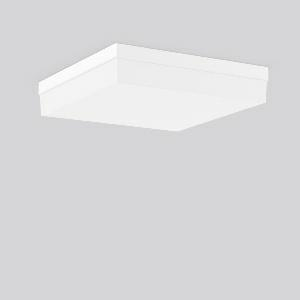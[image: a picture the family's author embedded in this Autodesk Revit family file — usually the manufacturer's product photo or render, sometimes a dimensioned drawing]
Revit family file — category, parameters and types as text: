
# Revit family: flat_quadrat_221162_002_1_f982
name_source: partatom
category: Lighting Fixtures
units: mm (PartAtom-declared; Revit-internal decimal feet)

## family parameters
Cut with Voids When Loaded = No
Host = Face
Light Source = No
Part Type = Normal
Room Calculation Point = No
Round Connector Dimension = Use Diameter
Shared = No

## types (1)
- FLAT QUADRAT (1 x LED Modul 840, 3650 lm, 4000)
    Apparent Load = 54 VA
    CIE Flux Codes = 42 72 91 88 100
    Color Rendering = 80
    Color Temperature = 4000
    Default Elevation = 1800 mm
    Description = Series: FLAT QUADRAT
Flat, square surface-mounted luminaire. Base: plastic. Diffuser: plastic (polypropylene), opal, satin finish. Diffuser fastening: spring system. IP 43 ceiling mounting, IP 44 wall mounting. 
Colour: white
Length: 470 mm
Width: 470 mm
Height: 100 mm
Lamp: LED
Socket: without socket
Colour temperature: 4000K
Colour rendering index (CRI): 83
System power: 54 W
Rated luminous flux: 3650 lm
Luminous efficiency: 68 lm/W
Control gear: Regulated power supply
Protection class: I
Type of protection: IP 43
    Height = 100 mm  [stored 0.328084 ft]
    Lamp = 1 x LED Modul 840
    Lamp Light Flux = 3650 lm
    Lamp count = 1
    Length = 470 mm
    Lifetime = 50000 h
    Luminous efficacy = 68 lm/W
    Manufacturer = RZB
    ModVariant = No
    Model = 221162.002.1
    Mounting Place = Ceiling, Wall
    Mounting Type = Surface mounted
    Number of Poles = 1
    OnlyDefault = Yes
    Power Factor = 1
    Product Name = FLAT QUADRAT
    Product group = Surface mounted ceiling and wall luminaires
    ProductGroupID = 305
    Protection Class = Protection class I
    Protection Degree = IP 43
    RLX_Detail_Level = 1
    RLX_Emergency_Light_Flux = 0 lm
    RLX_Emergency_Type = 0
    RLX_Emergency_Type_DB = No
    RlxData = <blob elided: 13965 chars, md5=58c8b692>
    Socket = socket
    Standby Power = 0 W
    System Light Flux = 3650 lm
    System Power = 54 W
    Type Comments = Product without accessories
    Type Image = 221080.862.79.jpg
    URL = http://relux.com
    VarID = ---
    Voltage = 230 V
    Voltage Range = 220-240 V
    Weight = 0.00 kg
    Width = 470 mm

note: [stored X ft] marks values corroborated as IEEE doubles in the binary element streams (Revit-internal decimal feet)

## geometry (parser evidence)
native form markers: Sweep x14
no freeform markers — native parametric forms only
